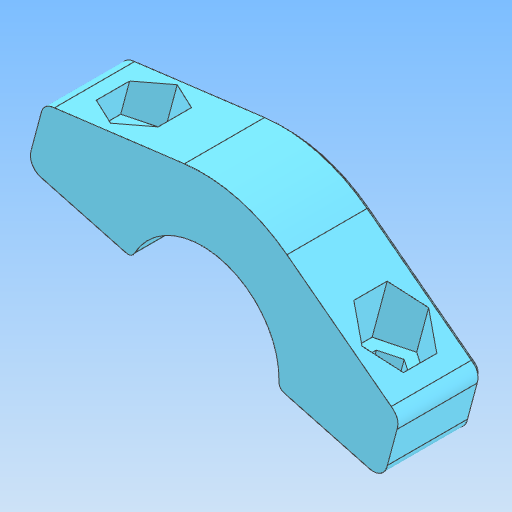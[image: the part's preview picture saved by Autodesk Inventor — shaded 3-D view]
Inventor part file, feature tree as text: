
AUTODESK INVENTOR PART (.ipt)
format: ipt  version: 2021.2 (Build 252289000, 289)  size: 263,680 bytes
history: native  units: mm
features: other x4, fillet x1, chamfer x1
ambient origin geometry x8: Origin, YZ Plane, XZ Plane, XY Plane, X Axis, Y Axis, Z Axis, Center Point
bodies: Body1 (feature_tree)
feature tree (6):
  other  "Твёрдое тело.ipt"
  fillet  "Сопряжение2"  Radius=10.0mm
  chamfer  "Фаска2"  Distance=1.0mm
  other  "Скобка 1::Твёрдое тело.ipt"
  other  "Элемент создания тегов1"
  other  "Твердое тело1"
